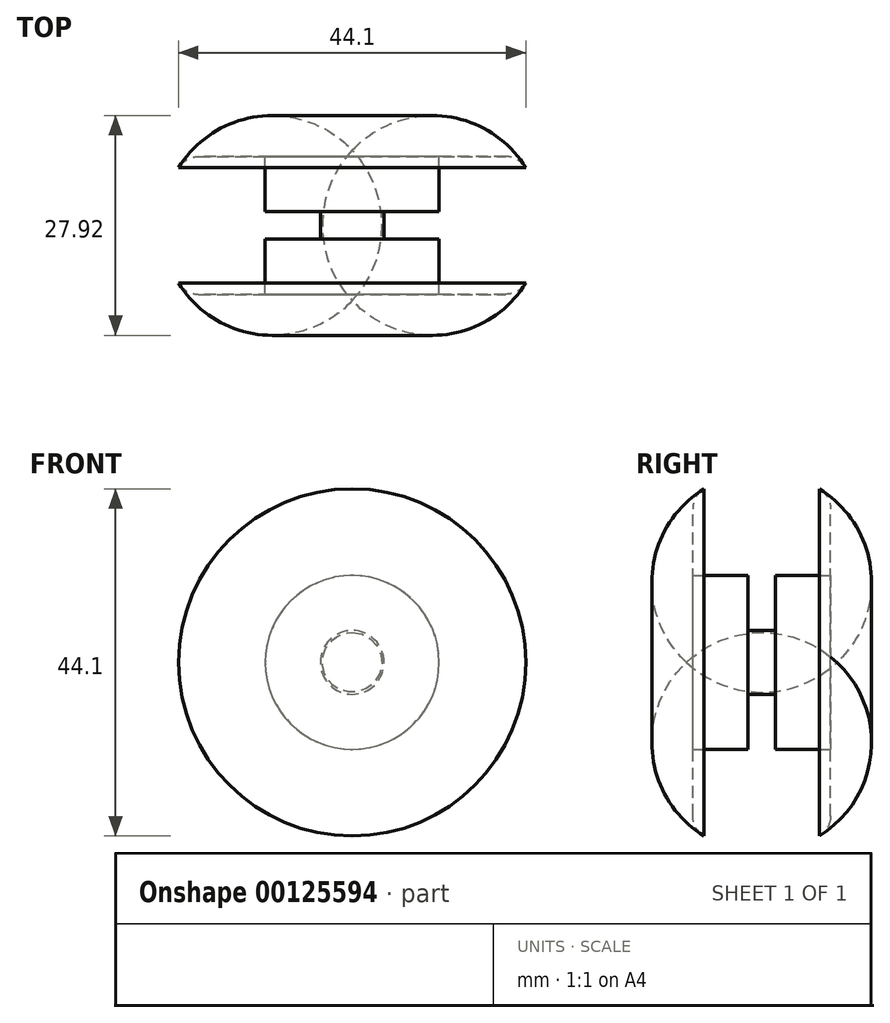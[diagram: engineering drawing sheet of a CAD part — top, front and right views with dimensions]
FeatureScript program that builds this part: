
annotation { "Feature Type Name" : "Feature", "Feature Type Description" : "" }
export const myFeature = defineFeature(function(context is Context, id is Id, definition is map)
    precondition{}
    {
        {
            var Q0;
            Q0=qCreatedBy(makeId("Top.planeOp"),FACE);
            var sketch = newSketch(context, id + "F0", { "sketchPlane" : qUnion([Q0])});
            skLineSegment(sketch, "E0.bottom", {"start": v(0, 0) * mm, "end": v(-19.5, 0) * mm});
            skLineSegment(sketch, "E0.top", {"start": v(0, 17.5) * mm, "end": v(-19.5, 17.5) * mm});
            skLineSegment(sketch, "E0.left", {"start": v(0, 0) * mm, "end": v(0, 17.5) * mm});
            skArc(sketch, "E1", {"start": v(-22.05, 16.07) * mm, "mid": v(-24.12, 8.75) * mm, "end": v(-22.05, 1.43) * mm});
            skPoint(sketch, "E1.centerSnap0", {"position": v(-24.12, 8.75) * mm});
            skPoint(sketch, "E2.orphan", {"position": v(-24.13, 17.5) * mm});
            skPoint(sketch, "E3.orphan", {"position": v(-24.12, 0) * mm});
            skPoint(sketch, "E4.visualSharp", {"position": v(-21.04, 17.5) * mm});
            skArc(sketch, "E4.filletArc", {"start": v(-19.5, 17.5) * mm, "mid": v(-20.96, 17.12) * mm, "end": v(-22.05, 16.07) * mm});
            skPoint(sketch, "E5.visualSharp", {"position": v(-21.04, 0) * mm});
            skArc(sketch, "E5.filletArc", {"start": v(-22.05, 1.43) * mm, "mid": v(-20.96, 0.38) * mm, "end": v(-19.5, 0) * mm});
            skSolve(sketch);
        }
        {
            var Q0;
            Q0=makeQuery(id+"F0.imprint","IMPRINT",FACE,{"disambiguationData":[TD([[makeQuery(id+"F0.imprint","IMPRINT",EDGE,{"derivedFrom":sQuery(id+"F0.wireOp",EDGE,"E0.bottom")}),-1.0]])]});
            var Q1;
            Q1=sQuery(id+"F0.wireOp",EDGE,"E0.left");
            revolve(context, id + "F1", {"entities" : qUnion([Q0]), "axis" : qUnion([Q1]), "revolveType" : RevolveType.FULL});
        }
        {
            var Q0;
            Q0=makeQuery(id+"F1.opRevolve","SWEPT_FACE",FACE,{"disambiguationData":[OSD([sQuery(id+"F0.wireOp",EDGE,"E0.top")])]});
            var sketch = newSketch(context, id + "F2", { "sketchPlane" : qUnion([Q0])});
            skCircle(sketch, "E6", {"center": v(0, 0) * mm, "radius": 11.05 * mm});
            skSolve(sketch);
        }
        {
            var Q0;
            Q0 = qSketchRegion(id + "F2", true);
            var Q1;
            Q1=makeQuery(id+"F2.imprint","IMPRINT",FACE,{"disambiguationData":[TD([[makeQuery(id+"F2.imprint","IMPRINT",EDGE,{"derivedFrom":sQuery(id+"F2.wireOp",EDGE,"E6")}),1.0]])]});
            extrude(context, id + "F3", {"entities" : qUnion([Q0, Q1]), "operationType" : NewBodyOperationType.REMOVE, "oppositeDirection" : true, "depth" : 25 * mm});
        }
        {
            var Q0;
            Q0=makeQuery(id+"F1.opRevolve","SWEPT_FACE",FACE,{"disambiguationData":[OSD([sQuery(id+"F0.wireOp",EDGE,"E0.bottom")])]});
            var Q1;
            Q1=makeQuery(id+"F1.opRevolve","SWEPT_FACE",FACE,{"disambiguationData":[OSD([sQuery(id+"F0.wireOp",EDGE,"E0.top")])]});
            cPlane(context, id + "F4", {"entities" : qUnion([Q0, Q1]), "cplaneType" : CPlaneType.MID_PLANE, "offset" : 25 * mm, "width" : 150 * mm, "height" : 150 * mm});
        }
        {
            var Q0;
            Q0=qCreatedBy(id+"F4.planeOp",FACE);
            var sketch = newSketch(context, id + "F5", { "sketchPlane" : qUnion([Q0])});
            skCircle(sketch, "E7", {"center": v(0, 0) * mm, "radius": 13.18 * mm});
            skCircle(sketch, "E8", {"center": v(0, 0) * mm, "radius": 4.05 * mm});
            skSolve(sketch);
        }
        {
            var Q0;
            Q0=makeQuery(id+"F5.imprint","IMPRINT",FACE,{"disambiguationData":[TD([[makeQuery(id+"F5.imprint","IMPRINT",EDGE,{"derivedFrom":sQuery(id+"F5.wireOp",EDGE,"E7")}),1.0]])]});
            extrude(context, id + "F6", {"entities" : qUnion([Q0]), "operationType" : NewBodyOperationType.ADD, "endBound" : BoundingType.SYMMETRIC, "depth" : 3.5 * mm});
        }
    });
